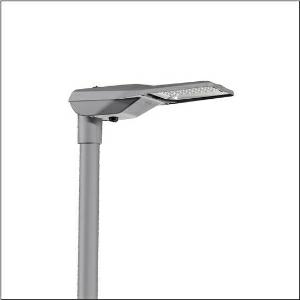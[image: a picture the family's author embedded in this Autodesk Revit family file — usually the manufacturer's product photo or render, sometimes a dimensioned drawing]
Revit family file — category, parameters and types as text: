
# Revit family: streetlight_sl_21_iq_mini___st1_0a_5xe2d41y08gb_5b29
name_source: partatom
category: Lighting Fixtures
units: mm (PartAtom-declared; Revit-internal decimal feet)

## family parameters
Cut with Voids When Loaded = No
Host = Face
Light Source = No
Part Type = Normal
Room Calculation Point = No
Round Connector Dimension = Use Diameter
Shared = No

## types (1)
- --- (1 x LED, 6190 lm, 39.8 W, 4000K)
    Apparent Load = 40 VA
    CIE Flux Codes = 37 72 97 100 100
    Color Rendering = 70
    Color Temperature = 4000K
    Default Elevation = 1800 mm
    Description = Streetlight SL 21 iQ mini, mast luminaire, primary light control with lens, of PMMA, primary optical cover: cover, of toughened safety glass, transparent, light distribution: ST1.0a, light emission: direct distribution, primary light characteristic: asymmetric, installation type: post-top, side-entry, LED, High Power LED, rated luminous flux: 6.190lm, luminous efficacy: 156lm/W, light colour: 740, colour temperature: 4000K, control gear: iQ-Street Remote, D4i with power reduction, control: pre-setting: logarithmic dimming characteristic, Street-Remote, Auto-Match, Temp-Guard, Lumen-Switch, Night-Set, Smart-Wire, Light-Fading, Desk-Remote (wireless, voltage-free reading and setting of iQ features in the workshop via application-optimized NFC function/RFID function), optimised constant luminous flux control (CLO 2.0), mains connection: 220..240V, AC, 50/60Hz, start of lifetime: 40W, end of service life: 41W, reduction: 18W, luminaire housing, of diecast aluminium, powder-coated, Siteco® metallic grey (DB 702S), corrosivity category C5 mid according to DIN EN ISO 12944, please order mast flange separately, inclination adjustable: 0°, 5°, 10°, 15°, sealing non-destructively replaceable, multi-level sealing system, length: 628mm, width: 235mm, height: 110mm, mast flange for spigot size: 42mm (side-entry): 5XC10008XM4, 60/48mm (side-entry/post-top): 5XC10108XM2, 76/60mm (side-entry/post-top): 5XC10108XM1, mounting height: 4..8m, Smart Interface below and above, protection rating (complete): IP66, insulation class (complete): insulation class II (safety insulation), certification: CE, ENEC, ENEC+, VDE, impact resistance: IK10, permissible operating ambient temperature for outdoor applications: -40..+50°C, standard-compliant lighting for roads and squares, packaging unit: 1 piece

Light Distribution: ST1.0a
    Height = 110 mm
    Lamp = 1 x LED
    Lamp Light Flux = 6190 lm
    Lamp Power = 39.8 W
    Lamp count = 1
    Length = 625 mm
    Luminous efficacy = 156 lm/W
    Manufacturer = Siteco
    ModVariant = No
    Model = 5XE2D41Y08GB
    Number of Poles = 1
    OnlyDefault = Yes
    Power Factor = 1
    Product Name = Streetlight SL 21 iQ mini | ST1.0a
    Product group = mast luminaire | pylon top
    ProductGroupID = 6100
    Protection Class = Protection class II
    Protection Degree = IP 66
    RLX_Detail_Level = 1
    RLX_Emergency_Light_Flux = 0 lm
    RLX_Emergency_Type = 0
    RLX_Emergency_Type_DB = No
    RlxData = <blob elided: 92589 chars, md5=c4bdcd7a>
    Socket = socket
    Standby Power = 0 W
    System Light Flux = 6190 lm
    System Power = 40 W
    Type Comments = factory setting: luminous flux: 100 % | dim-lin: 254 | 800 mA
    Type Image = l_1003514.jpg
    URL = http://relux.com
    VarID = @adj_136235
    Voltage = 0 V
    Weight = 0.00 kg
    Width = 234 mm

## geometry (parser evidence)
native form markers: Blend x4, Sweep x11
no freeform markers — native parametric forms only
